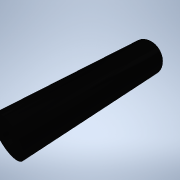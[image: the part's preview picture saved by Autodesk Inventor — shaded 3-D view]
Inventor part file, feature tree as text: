
AUTODESK INVENTOR PART (.ipt)
format: ipt  version: 2020 (Build 240168000, 168)  size: 94,208 bytes
history: native  units: mm
features: extrude x1, sketch x1
ambient origin geometry x8: Origin, YZ Plane, XZ Plane, XY Plane, X Axis, Y Axis, Z Axis, Center Point
bodies: Solid1 (feature_tree)
feature tree (2):
  extrude  "Extrusion1"  Depth=50.0mm
  sketch  "Sketch1"  dims[d0=4.0mm d1=12.0mm d2=50.0mm d3=0.0mm]
